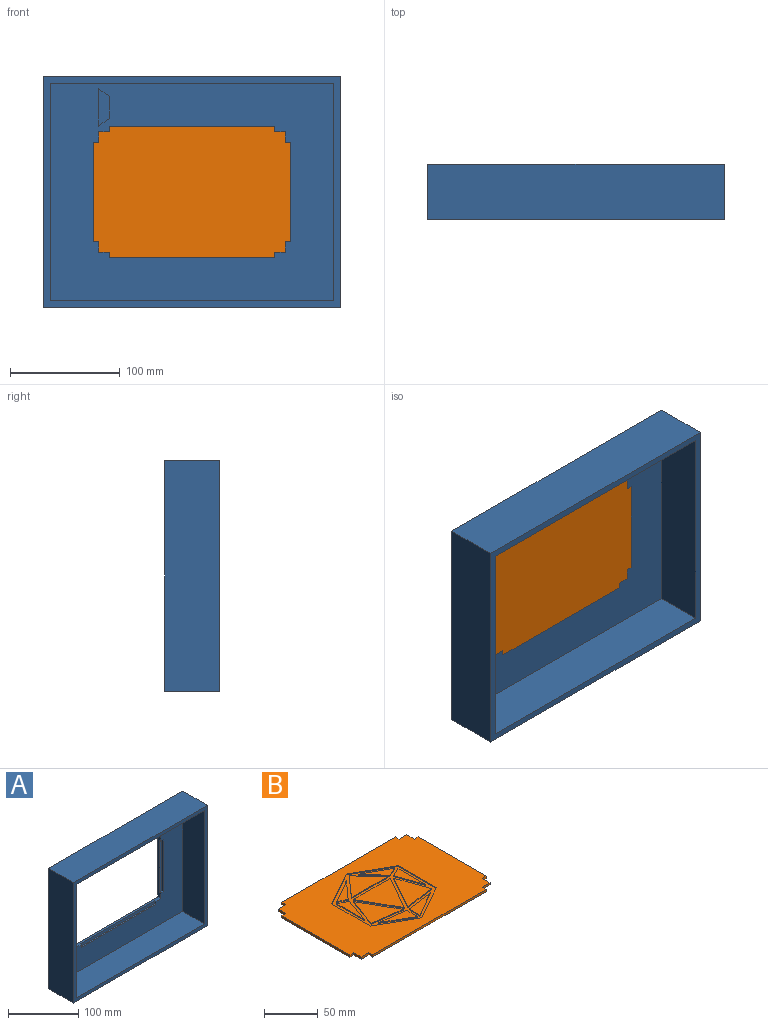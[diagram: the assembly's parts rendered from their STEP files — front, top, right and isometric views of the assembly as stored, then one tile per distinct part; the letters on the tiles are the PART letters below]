
ASSEMBLY  parts=2 mates=1
PART A: 41 faces, bbox 270x50x210 mm
  f0: plane 34x2mm, normal (1,0,0), area 68mm2, adj f1,f3,f25,f40
  f1: plane 10x7mm, normal (-0.57,0,-0.82), area 24.4mm2, adj f0,f2,f25,f40
  f2: plane 20x2mm, normal (-1,0,0), area 40mm2, adj f1,f3,f25,f40
  f3: plane 10x7mm, normal (-0.57,0,0.82), area 24.4mm2, adj f0,f2,f25,f40
  f4: plane 34x2mm, normal (1,0,0), area 68mm2, adj f5,f23,f24,f39
  f5: plane 10x7mm, normal (-0.57,0,-0.82), area 24.4mm2, adj f4,f6,f24,f39
  f6: plane 20x2mm, normal (-1,0,0), area 40mm2, adj f5,f23,f24,f39
  f7: plane 5x2.5mm, normal (0,0,-1), area 12.5mm2, adj f8,f10,f24,f36
  f8: plane 90x2.5mm, normal (-1,0,0), area 225mm2, adj f7,f9,f24,f36
  f9: plane 5x2.5mm, normal (0,0,1), area 12.5mm2, adj f8,f10,f24,f36
  f10: plane 110x6mm, normal (-1,0,0), area 435mm2, adj f7,f9,f14,f19,f24,f25,f36
  f11: plane 5x2.5mm, normal (-1,0,0), area 12.5mm2, adj f12,f14,f24,f38
  f12: plane 150x2.5mm, normal (0,0,1), area 375mm2, adj f11,f13,f24,f38
  f13: plane 5x2.5mm, normal (1,0,0), area 12.5mm2, adj f12,f14,f24,f38
  f14: plane 170x6mm, normal (0,0,1), area 645mm2, adj f10,f11,f13,f18,f24,f25,f38
  f15: plane 5x2.5mm, normal (0,0,1), area 12.5mm2, adj f16,f18,f24,f35
  f16: plane 90x2.5mm, normal (1,0,0), area 225mm2, adj f15,f17,f24,f35
  f17: plane 5x2.5mm, normal (0,0,-1), area 12.5mm2, adj f16,f18,f24,f35
  f18: plane 110x6mm, normal (1,0,0), area 435mm2, adj f14,f15,f17,f19,f24,f25,f35
  f19: plane 170x6mm, normal (0,0,-1), area 645mm2, adj f10,f18,f20,f22,f24,f25,f37
  f20: plane 5x2.5mm, normal (1,0,0), area 12.5mm2, adj f19,f21,f24,f37
  f21: plane 150x2.5mm, normal (0,0,-1), area 375mm2, adj f20,f22,f24,f37
  f22: plane 5x2.5mm, normal (-1,0,0), area 12.5mm2, adj f19,f21,f24,f37
  f23: plane 10x7mm, normal (-0.57,0,0.82), area 24.4mm2, adj f4,f6,f24,f39
  f24: plane 258x198mm, normal (0,-1,0), area 29714mm2, adj f4,f5,f6,f7,f8,f9,f10,f11
  f25: plane 270x210mm, normal (0,1,0), area 37730mm2, adj f0,f1,f2,f3,f10,f14,f18,f19
  f26: plane 198x44mm, normal (1,0,0), area 8712mm2, adj f24,f27,f29,f34
  f27: plane 258x44mm, normal (0,0,1), area 11352mm2, adj f24,f26,f28,f34
  f28: plane 198x44mm, normal (-1,0,0), area 8712mm2, adj f24,f27,f29,f34
  f29: plane 258x44mm, normal (0,0,-1), area 11352mm2, adj f24,f26,f28,f34
  f30: plane 210x50mm, normal (-1,0,0), area 10500mm2, adj f25,f31,f33,f34
  f31: plane 270x50mm, normal (0,0,-1), area 13500mm2, adj f25,f30,f32,f34
  f32: plane 210x50mm, normal (1,0,0), area 10500mm2, adj f25,f31,f33,f34
  f33: plane 270x50mm, normal (0,0,1), area 13500mm2, adj f25,f30,f32,f34
  f34: plane 270x210mm, normal (0,-1,0), area 5616mm2, adj f26,f27,f28,f29,f30,f31,f32,f33
  f35: plane 90x5mm, normal (0,-1,0), area 450mm2, adj f15,f16,f17,f18
  f36: plane 90x5mm, normal (0,-1,0), area 450mm2, adj f7,f8,f9,f10
  f37: plane 150x5mm, normal (0,-1,0), area 750mm2, adj f19,f20,f21,f22
  f38: plane 150x5mm, normal (0,-1,0), area 750mm2, adj f11,f12,f13,f14
  f39: plane 34x10mm, normal (0,-1,0), area 270mm2, adj f4,f5,f6,f23
  f40: plane 34x10mm, normal (0,1,0), area 270mm2, adj f0,f1,f2,f3
PART B: 69 faces, bbox 180x120x2.5 mm
  f0: plane 180x120mm, normal (0,0,1), area 14497mm2, adj f1,f2,f3,f4,f5,f6,f7,f8
  f1: plane 5x2.5mm, normal (-1,0,0), area 12.5mm2, adj f0,f2,f20,f21
  f2: plane 10x2.5mm, normal (0,1,0), area 25mm2, adj f0,f1,f3,f21
  f3: plane 10x2.5mm, normal (-1,0,0), area 25mm2, adj f0,f2,f4,f21
  f4: plane 5x2.5mm, normal (0,1,0), area 12.5mm2, adj f0,f3,f5,f21
  f5: plane 90x2.5mm, normal (-1,0,0), area 225mm2, adj f0,f4,f6,f21
  f6: plane 5x2.5mm, normal (0,-1,0), area 12.5mm2, adj f0,f5,f7,f21
  f7: plane 10x2.5mm, normal (-1,0,0), area 25mm2, adj f0,f6,f8,f21
  f8: plane 10x2.5mm, normal (0,-1,0), area 25mm2, adj f0,f7,f9,f21
  f9: plane 5x2.5mm, normal (-1,0,0), area 12.5mm2, adj f0,f8,f10,f21
  f10: plane 150x2.5mm, normal (0,-1,0), area 375mm2, adj f0,f9,f11,f21
  f11: plane 5x2.5mm, normal (1,0,0), area 12.5mm2, adj f0,f10,f12,f21
  f12: plane 10x2.5mm, normal (0,-1,0), area 25mm2, adj f0,f11,f13,f21
  f13: plane 10x2.5mm, normal (1,0,0), area 25mm2, adj f0,f12,f14,f21
  f14: plane 5x2.5mm, normal (0,-1,0), area 12.5mm2, adj f0,f13,f15,f21
  f15: plane 90x2.5mm, normal (1,0,0), area 225mm2, adj f0,f14,f16,f21
  f16: plane 5x2.5mm, normal (0,1,0), area 12.5mm2, adj f0,f15,f17,f21
  f17: plane 10x2.5mm, normal (1,0,0), area 25mm2, adj f0,f16,f18,f21
  f18: plane 10x2.5mm, normal (0,1,0), area 25mm2, adj f0,f17,f19,f21
  f19: plane 5x2.5mm, normal (1,0,0), area 12.5mm2, adj f0,f18,f20,f21
  f20: plane 150x2.5mm, normal (0,1,0), area 375mm2, adj f0,f1,f19,f21
  f21: plane 180x120mm, normal (0,0,-1), area 21100mm2, adj f1,f2,f3,f4,f5,f6,f7,f8
  f22: plane 42.75x24.36mm, normal (-0.87,-0.5,0), area 49.2mm2, adj f23,f57,f58,f68
  f23: plane 48.73x1mm, normal (0,1,0), area 48.7mm2, adj f22,f57,f58,f68
  f24: plane 36.84x5.25mm, normal (0.14,-0.99,0), area 37.2mm2, adj f25,f47,f58,f67
  f25: plane 41.94x23.91mm, normal (-0.87,0.5,0), area 48.3mm2, adj f24,f47,f58,f67
  f26: plane 30.2x17.49mm, normal (-0.5,0.87,0), area 34.9mm2, adj f27,f48,f58,f66
  f27: plane 22.07x19.88mm, normal (0.74,-0.67,0), area 29.7mm2, adj f26,f48,f58,f66
  f28: plane 32.36x18.67mm, normal (0.5,-0.87,0), area 37.4mm2, adj f29,f49,f58,f65
  f29: plane 14.25x1mm, normal (-1,0,0), area 14.3mm2, adj f28,f49,f58,f65
  f30: plane 43.67x24.55mm, normal (0.49,0.87,0), area 50.1mm2, adj f0,f31,f50,f58
  f31: plane 43.89x24.55mm, normal (-0.49,0.87,0), area 50.3mm2, adj f0,f30,f32,f58
  f32: plane 50.69x1mm, normal (-1,0,0), area 50.7mm2, adj f0,f31,f33,f58
  f33: plane 44.04x24.76mm, normal (-0.49,-0.87,0), area 50.5mm2, adj f0,f32,f34,f58
  f34: plane 43.66x24.76mm, normal (0.49,-0.87,0), area 50.2mm2, adj f0,f33,f50,f58
  f35: plane 14.19x1mm, normal (1,0,0), area 14.2mm2, adj f36,f51,f58,f64
  f36: plane 32.42x18.67mm, normal (-0.5,-0.87,0), area 37.4mm2, adj f35,f51,f58,f64
  f37: plane 11.16x5.05mm, normal (-0.41,0.91,0), area 12.2mm2, adj f38,f52,f58,f63
  f38: plane 36.52x1mm, normal (1,0,0), area 36.5mm2, adj f37,f52,f58,f63
  f39: plane 22.27x19.78mm, normal (-0.75,-0.66,0), area 29.8mm2, adj f40,f53,f58,f62
  f40: plane 30.77x17.3mm, normal (0.49,0.87,0), area 35.3mm2, adj f39,f53,f58,f62
  f41: plane 26.47x23.41mm, normal (-0.75,0.66,0), area 35.3mm2, adj f42,f54,f58,f61
  f42: plane 26.47x23.79mm, normal (0.74,0.67,0), area 35.6mm2, adj f41,f54,f58,f61
  f43: plane 36.56x13.03mm, normal (-0.94,0.34,0), area 38.8mm2, adj f44,f55,f58,f60
  f44: plane 41.8x23.93mm, normal (0.87,0.5,0), area 48.2mm2, adj f43,f55,f58,f60
  f45: plane 36.52x1mm, normal (-1,0,0), area 36.5mm2, adj f46,f56,f58,f59
  f46: plane 11.22x5.05mm, normal (0.41,0.91,0), area 12.3mm2, adj f45,f56,f58,f59
  f47: plane 36.69x12.93mm, normal (0.94,0.33,0), area 38.9mm2, adj f24,f25,f58,f67
  f48: plane 10.32x4.59mm, normal (-0.41,-0.91,0), area 11.3mm2, adj f26,f27,f58,f66
  f49: plane 32.36x4.42mm, normal (-0.14,0.99,0), area 32.7mm2, adj f28,f29,f58,f65
  f50: plane 50.69x1mm, normal (1,0,0), area 50.7mm2, adj f0,f30,f34,f58
  f51: plane 32.42x4.48mm, normal (0.14,0.99,0), area 32.7mm2, adj f35,f36,f58,f64
  f52: plane 31.47x11.07mm, normal (-0.94,-0.33,0), area 33.4mm2, adj f37,f38,f58,f63
  f53: plane 10.99x4.97mm, normal (0.41,-0.91,0), area 12.1mm2, adj f39,f40,f58,f62
  f54: plane 47.21x1mm, normal (0,-1,0), area 47.2mm2, adj f41,f42,f58,f61
  f55: plane 36.96x5.24mm, normal (-0.14,-0.99,0), area 37.3mm2, adj f43,f44,f58,f60
  f56: plane 31.47x11.22mm, normal (0.94,-0.34,0), area 33.4mm2, adj f45,f46,f58,f59
  f57: plane 42.75x24.36mm, normal (0.87,-0.5,0), area 49.2mm2, adj f22,f23,f58,f68
  f58: plane 100x87.7mm, normal (0,0,1), area 2317.2mm2, adj f22,f23,f24,f25,f26,f27,f28,f29
  f59: plane 36.52x11.22mm, normal (0,0,1), area 204.9mm2, adj f45,f46,f56
  f60: plane 41.8x36.96mm, normal (0,0,1), area 709.8mm2, adj f43,f44,f55
  f61: plane 47.21x26.47mm, normal (0,0,1), area 624.8mm2, adj f41,f42,f54
  f62: plane 30.77x22.27mm, normal (0,0,1), area 171.5mm2, adj f39,f40,f53
  f63: plane 36.52x11.16mm, normal (0,0,1), area 203.6mm2, adj f37,f38,f52
  f64: plane 32.42x18.67mm, normal (0,0,1), area 230mm2, adj f35,f36,f51
  f65: plane 32.36x18.67mm, normal (0,0,1), area 230.6mm2, adj f28,f29,f49
  f66: plane 30.2x22.07mm, normal (0,0,1), area 159.5mm2, adj f26,f27,f48
  f67: plane 41.94x36.84mm, normal (0,0,1), area 709.8mm2, adj f24,f25,f47
  f68: plane 48.73x42.75mm, normal (0,0,1), area 1041.5mm2, adj f22,f23,f57
PLACE A rot(axis=(-0.04,-0.09,-0.99),0deg) t=(211.79,-135.32,-78.58)mm
PLACE B rot(axis=(0,0.71,0.71),180deg) t=(307.53,-141.32,-121.53)mm
MATE fastened A.f37 <-> B.f0  axis (0,-1,0) through (211.79,-138.82,-18.58)mm
